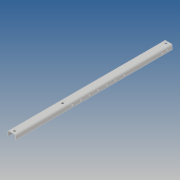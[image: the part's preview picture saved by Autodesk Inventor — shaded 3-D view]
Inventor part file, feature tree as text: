
AUTODESK INVENTOR PART (.ipt)
format: ipt  version: 2019 (Build 230136000, 136)  size: 155,648 bytes
history: native  units: mm
features: sketch x6, other x5, hole x4, sheet_metal_op x1, pattern_linear x1, projected_geometry x1
ambient origin geometry x8: Origin, YZ Plane, XZ Plane, XY Plane, X Axis, Y Axis, Z Axis, Center Point
bodies: Body1 (feature_tree)
feature tree (18):
  sheet_metal_op  "Face2"
  other  "Bord tombé2"
  hole  "Perçage2"  [1 undecoded]
  hole  "Perçage3"  [1 undecoded]
  hole  "Perçage4"  [1 undecoded]
  hole  "Perçage5"  [1 undecoded]
  pattern_linear  "Réseau rectangulaire2"  Spacing1=0.5mm  [1 undecoded]
  sketch  "Esquisse4"
  other  "Plaque3"
  sketch  "Esquisse5"
  other  "Plaque4"
  other  "Pli2"
  other  "Coin2"
  sketch  "Esquisse6"
  sketch  "Esquisse7"
  sketch  "Esquisse8"
  projected_geometry  "Boucle projetée1"
  sketch  "Esquisse9"
note: 5 required parameter values undecoded (feature->parameter linkage not recoverable at this tier; creation-order binding heuristic only, values carry confidence <= 0.55)
